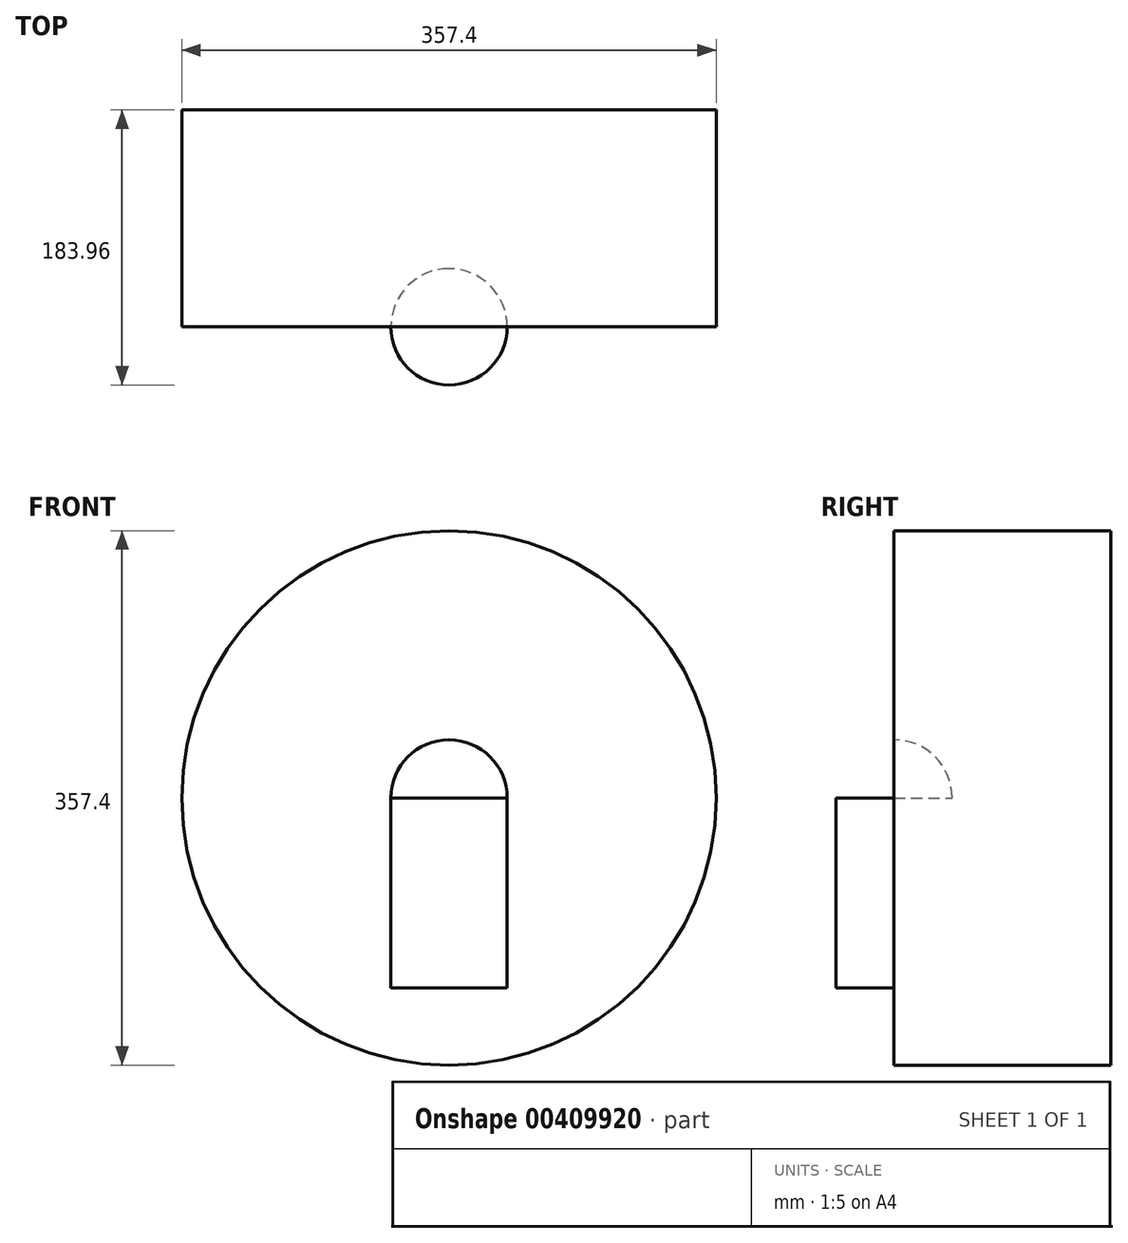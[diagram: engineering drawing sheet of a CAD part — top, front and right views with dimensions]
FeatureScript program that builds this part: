
annotation { "Feature Type Name" : "Feature", "Feature Type Description" : "" }
export const myFeature = defineFeature(function(context is Context, id is Id, definition is map)
    precondition{}
    {
        {
            var Q0;
            Q0=qCreatedBy(makeId("Top.planeOp"),FACE);
            var sketch = newSketch(context, id + "F0", { "sketchPlane" : qUnion([Q0])});
            skCircle(sketch, "E0", {"center": v(0, 0) * mm, "radius": 38.92 * mm});
            skSolve(sketch);
        }
        {
            var Q0;
            Q0=makeQuery(id+"F0.imprint","IMPRINT",FACE,{"disambiguationData":[TD([[makeQuery(id+"F0.imprint","IMPRINT",EDGE,{"derivedFrom":sQuery(id+"F0.wireOp",EDGE,"E0")}),1.0]])]});
            extrude(context, id + "F1", {"entities" : qUnion([Q0]), "depth" : 127 * mm, "offsetDistance" : 25.4 * mm});
        }
        {
            var Q0;
            Q0=makeQuery(id+"F1.opExtrude","CAP_FACE",FACE,{"disambiguationData":[OSD([sQuery(id+"F0.wireOp",EDGE,"E0")])],"isStart":false});
            var sketch = newSketch(context, id + "F2", { "sketchPlane" : qUnion([Q0])});
            skLineSegment(sketch, "E1.bottom", {"start": v(0, 0) * mm, "end": v(178.7, 0) * mm});
            skLineSegment(sketch, "E1.top", {"start": v(0, 145.04) * mm, "end": v(178.7, 145.04) * mm});
            skLineSegment(sketch, "E1.left", {"start": v(0, 0) * mm, "end": v(0, 145.04) * mm});
            skLineSegment(sketch, "E1.right", {"start": v(178.7, 0) * mm, "end": v(178.7, 145.04) * mm});
            skLineSegment(sketch, "E2", {"start": v(0, 217.4) * mm, "end": v(0, 0) * mm, "construction": true});
            skSolve(sketch);
        }
        {
            var Q0;
            {var subQ2=sQuery(id+"F2.wireOp",EDGE,"E1.top");Q0=makeQuery(id+"F2.imprint","IMPRINT",FACE,{"disambiguationData":[TD([[makeQuery(id+"F2.imprint","IMPRINT",EDGE,{"derivedFrom":subQ2}),-1.0]])]});}
            var Q1;
            Q1=sQuery(id+"F2.wireOp",EDGE,"E2");
            revolve(context, id + "F3", {"operationType" : NewBodyOperationType.ADD, "surfaceOperationType" : NewSurfaceOperationType.NEW, "entities" : qUnion([Q0]), "axis" : qUnion([Q1]), "revolveType" : RevolveType.FULL});
        }
    });
